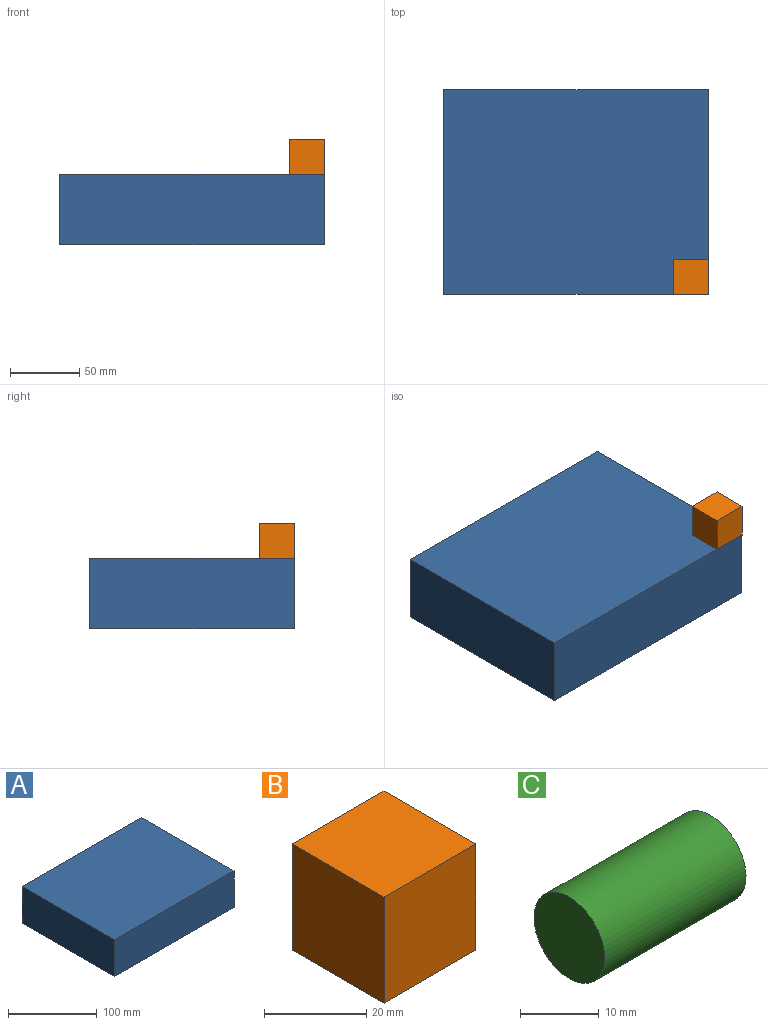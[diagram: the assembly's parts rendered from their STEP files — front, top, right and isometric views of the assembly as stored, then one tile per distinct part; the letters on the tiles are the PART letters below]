
ASSEMBLY  parts=3 mates=2
PART A: 8 faces, bbox 190.8x147.7x50.8 mm
  f0: plane 190.84x50.8mm, normal (0,1,0), area 9694.9mm2, adj f1,f3,f4,f5
  f1: plane 147.74x50.8mm, normal (-1,0,0), area 7505mm2, adj f0,f2,f4,f5
  f2: plane 190.84x50.8mm, normal (0,-1,0), area 9694.9mm2, adj f1,f3,f4,f5
  f3: plane 147.74x50.8mm, normal (1,0,0), area 6977.9mm2, adj f0,f2,f4,f5,f6
  f4: plane 190.84x147.74mm, normal (0,0,1), area 28194.7mm2, adj f0,f1,f2,f3
  f5: plane 190.84x147.74mm, normal (0,0,-1), area 28194.7mm2, adj f0,f1,f2,f3
  f6: cylinder r=12.95mm len=25.91mm, axis (1,0,0), area 2067.3mm2, adj f3,f7
  f7: plane 25.91x25.91mm, normal (1,0,0), area 527.1mm2, adj f6
PART B: 6 faces, bbox 25.4x25.4x25.4 mm
  f0: plane 25.4x25.4mm, normal (0,1,0), area 645.2mm2, adj f1,f3,f4,f5
  f1: plane 25.4x25.4mm, normal (-1,0,0), area 645.2mm2, adj f0,f2,f4,f5
  f2: plane 25.4x25.4mm, normal (0,-1,0), area 645.2mm2, adj f1,f3,f4,f5
  f3: plane 25.4x25.4mm, normal (1,0,0), area 645.2mm2, adj f0,f2,f4,f5
  f4: plane 25.4x25.4mm, normal (0,0,1), area 645.2mm2, adj f0,f1,f2,f3
  f5: plane 25.4x25.4mm, normal (0,0,-1), area 645.2mm2, adj f0,f1,f2,f3
PART C: 3 faces, bbox 25.4x12.7x12.7 mm
  f0: cylinder r=6.35mm len=25.4mm, axis (-1,0,0), area 1013.4mm2, adj f1,f2
  f1: plane 12.7x12.7mm, normal (1,0,0), area 126.7mm2, adj f0
  f2: plane 12.7x12.7mm, normal (-1,0,0), area 126.7mm2, adj f0
PLACE A t=(78.07,-1.53,97.72)mm
PLACE B t=(105.83,-46.51,148.52)mm
PLACE C t=(117.05,27.08,124.23)mm
MATE fastened A.f6 <-> C.f0  axis (1,0,0) through (117.05,27.08,124.23)mm
MATE fastened B.f5 <-> A.f4  axis (0,0,-1) through (142.45,-53.65,148.52)mm
